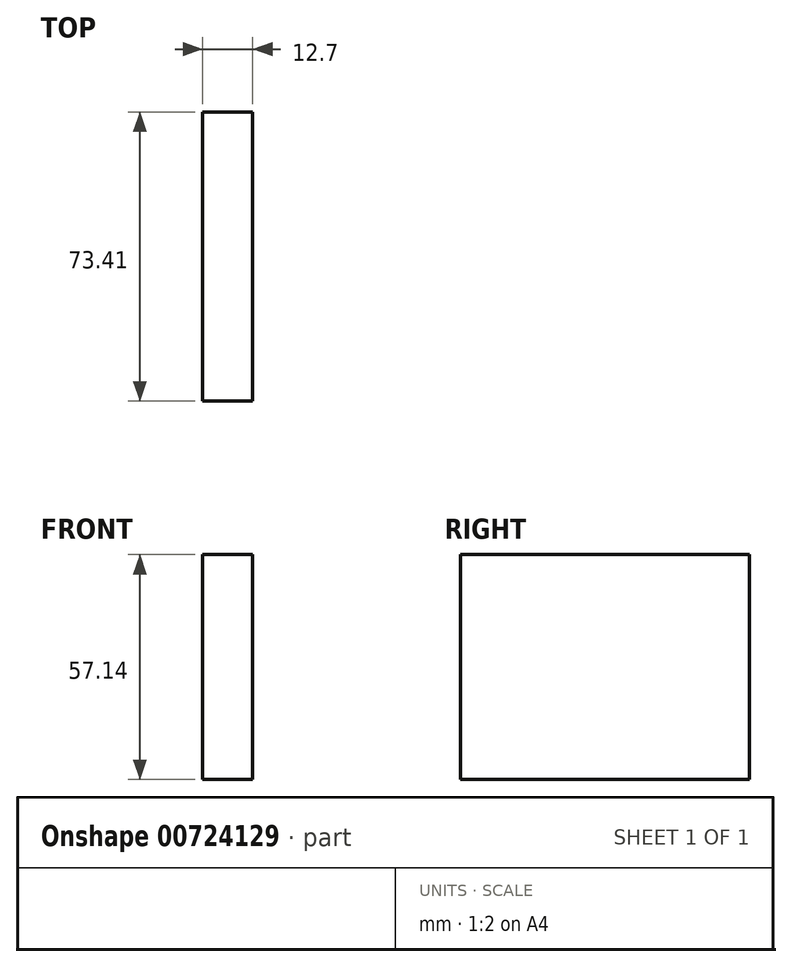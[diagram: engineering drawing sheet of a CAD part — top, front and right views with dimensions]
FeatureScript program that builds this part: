
annotation { "Feature Type Name" : "Feature", "Feature Type Description" : "" }
export const myFeature = defineFeature(function(context is Context, id is Id, definition is map)
    precondition{}
    {
        {
            var Q0;
            Q0=qCreatedBy(makeId("Right.planeOp"),FACE);
            var sketch = newSketch(context, id + "F0", { "sketchPlane" : qUnion([Q0])});
            skLineSegment(sketch, "E0.bottom", {"start": v(33.34, 0) * mm, "end": v(-40.07, 0) * mm});
            skLineSegment(sketch, "E0.top", {"start": v(33.34, -28.57) * mm, "end": v(-40.07, -28.58) * mm});
            skLineSegment(sketch, "E0.left", {"start": v(33.34, 0) * mm, "end": v(33.34, -28.57) * mm});
            skLineSegment(sketch, "E0.right", {"start": v(-40.07, 0) * mm, "end": v(-40.07, -28.58) * mm});
            skLineSegment(sketch, "E1.bottom", {"start": v(-40.07, -28.58) * mm, "end": v(36.13, -28.57) * mm});
            skLineSegment(sketch, "E1.top", {"start": v(-40.07, -57.02) * mm, "end": v(36.13, -57.02) * mm});
            skLineSegment(sketch, "E1.left", {"start": v(-40.07, -28.58) * mm, "end": v(-40.07, -57.02) * mm});
            skLineSegment(sketch, "E2.top", {"start": v(36.13, -57.02) * mm, "end": v(64.58, -57.02) * mm});
            skLineSegment(sketch, "E3.bottom", {"start": v(-40.07, -28.58) * mm, "end": v(-33.72, -28.58) * mm});
            skLineSegment(sketch, "E3.top", {"start": v(-40.07, -57.02) * mm, "end": v(-33.72, -57.02) * mm});
            skLineSegment(sketch, "E3.right", {"start": v(-33.72, -28.58) * mm, "end": v(-33.72, -57.02) * mm});
            skLineSegment(sketch, "E4", {"start": v(36.13, -42.8) * mm, "end": v(-33.72, -42.8) * mm});
            skLineSegment(sketch, "E5", {"start": v(-33.72, -42.8) * mm, "end": v(-40.07, -42.8) * mm});
            skLineSegment(sketch, "E6", {"start": v(-15.43, -28.57) * mm, "end": v(-15.43, -57.02) * mm});
            skLineSegment(sketch, "E7", {"start": v(36.13, -28.57) * mm, "end": v(64.58, -57.02) * mm});
            skLineSegment(sketch, "E8", {"start": v(29.53, -42.8) * mm, "end": v(29.53, -57.02) * mm});
            skLineSegment(sketch, "E9", {"start": v(36.13, -42.8) * mm, "end": v(50.35, -42.8) * mm});
            skLineSegment(sketch, "E10", {"start": v(36.13, -28.57) * mm, "end": v(71.16, -28.57) * mm, "construction": true});
            skCircle(sketch, "E11", {"center": v(-15.43, -42.8) * mm, "radius": 5.25 * mm});
            skCircle(sketch, "E12", {"center": v(14.52, -42.8) * mm, "radius": 5.25 * mm});
            skLineSegment(sketch, "E13.MirrorCS", {"start": v(-40.07, 28.58) * mm, "end": v(-33.72, 28.58) * mm});
            skLineSegment(sketch, "E14.MirrorCS", {"start": v(-40.07, 57.02) * mm, "end": v(-33.72, 57.02) * mm});
            skLineSegment(sketch, "E15.MirrorCS", {"start": v(36.13, 57.02) * mm, "end": v(64.58, 57.02) * mm});
            skLineSegment(sketch, "E16.MirrorCS", {"start": v(-33.72, 42.8) * mm, "end": v(-40.07, 42.8) * mm});
            skLineSegment(sketch, "E17.MirrorCS", {"start": v(33.34, 28.57) * mm, "end": v(-40.07, 28.58) * mm});
            skLineSegment(sketch, "E18.MirrorCS", {"start": v(-40.07, 28.58) * mm, "end": v(-40.07, 57.02) * mm});
            skLineSegment(sketch, "E19.MirrorCS", {"start": v(36.13, 42.8) * mm, "end": v(-33.72, 42.8) * mm});
            skCircle(sketch, "E20.MirrorC", {"center": v(-15.43, 42.8) * mm, "radius": 5.25 * mm});
            skLineSegment(sketch, "E21.MirrorCS", {"start": v(36.13, 28.57) * mm, "end": v(71.16, 28.57) * mm, "construction": true});
            skLineSegment(sketch, "E22.MirrorCS", {"start": v(36.13, 28.57) * mm, "end": v(64.58, 57.02) * mm});
            skCircle(sketch, "E23.MirrorC", {"center": v(14.52, 42.8) * mm, "radius": 5.25 * mm});
            skLineSegment(sketch, "E24.MirrorCS", {"start": v(-15.43, 28.57) * mm, "end": v(-15.43, 57.02) * mm});
            skLineSegment(sketch, "E25.MirrorCS", {"start": v(-33.72, 28.58) * mm, "end": v(-33.72, 57.02) * mm});
            skLineSegment(sketch, "E26.MirrorCS", {"start": v(29.53, 42.8) * mm, "end": v(29.53, 57.02) * mm});
            skLineSegment(sketch, "E27.MirrorCS", {"start": v(-40.07, 28.58) * mm, "end": v(36.13, 28.57) * mm});
            skLineSegment(sketch, "E28.MirrorCS", {"start": v(36.13, 42.8) * mm, "end": v(50.35, 42.8) * mm});
            skLineSegment(sketch, "E29.MirrorCS", {"start": v(-40.07, 57.02) * mm, "end": v(36.13, 57.02) * mm});
            skLineSegment(sketch, "E30.MirrorCS", {"start": v(-40.07, 0) * mm, "end": v(-40.07, 28.58) * mm});
            skLineSegment(sketch, "E31.MirrorCS", {"start": v(33.34, 0) * mm, "end": v(33.34, 28.57) * mm});
            skSolve(sketch);
        }
        {
            var Q0;
            Q0=makeQuery(id+"F0.imprint","IMPRINT",FACE,{"disambiguationData":[TD([[makeQuery(id+"F0.imprint","IMPRINT",EDGE,{"derivedFrom":sQuery(id+"F0.wireOp",EDGE,"E0.bottom")}),-1.0]])]});
            var Q1;
            Q1=makeQuery(id+"F0.imprint","IMPRINT",FACE,{"disambiguationData":[TD([[makeQuery(id+"F0.imprint","IMPRINT",EDGE,{"derivedFrom":sQuery(id+"F0.wireOp",EDGE,"E0.bottom")}),1.0]])]});
            extrude(context, id + "F1", {"entities" : qUnion([Q0, Q1]), "oppositeDirection" : true, "depth" : 12.7 * mm, "offsetDistance" : 25.4 * mm});
        }
    });
